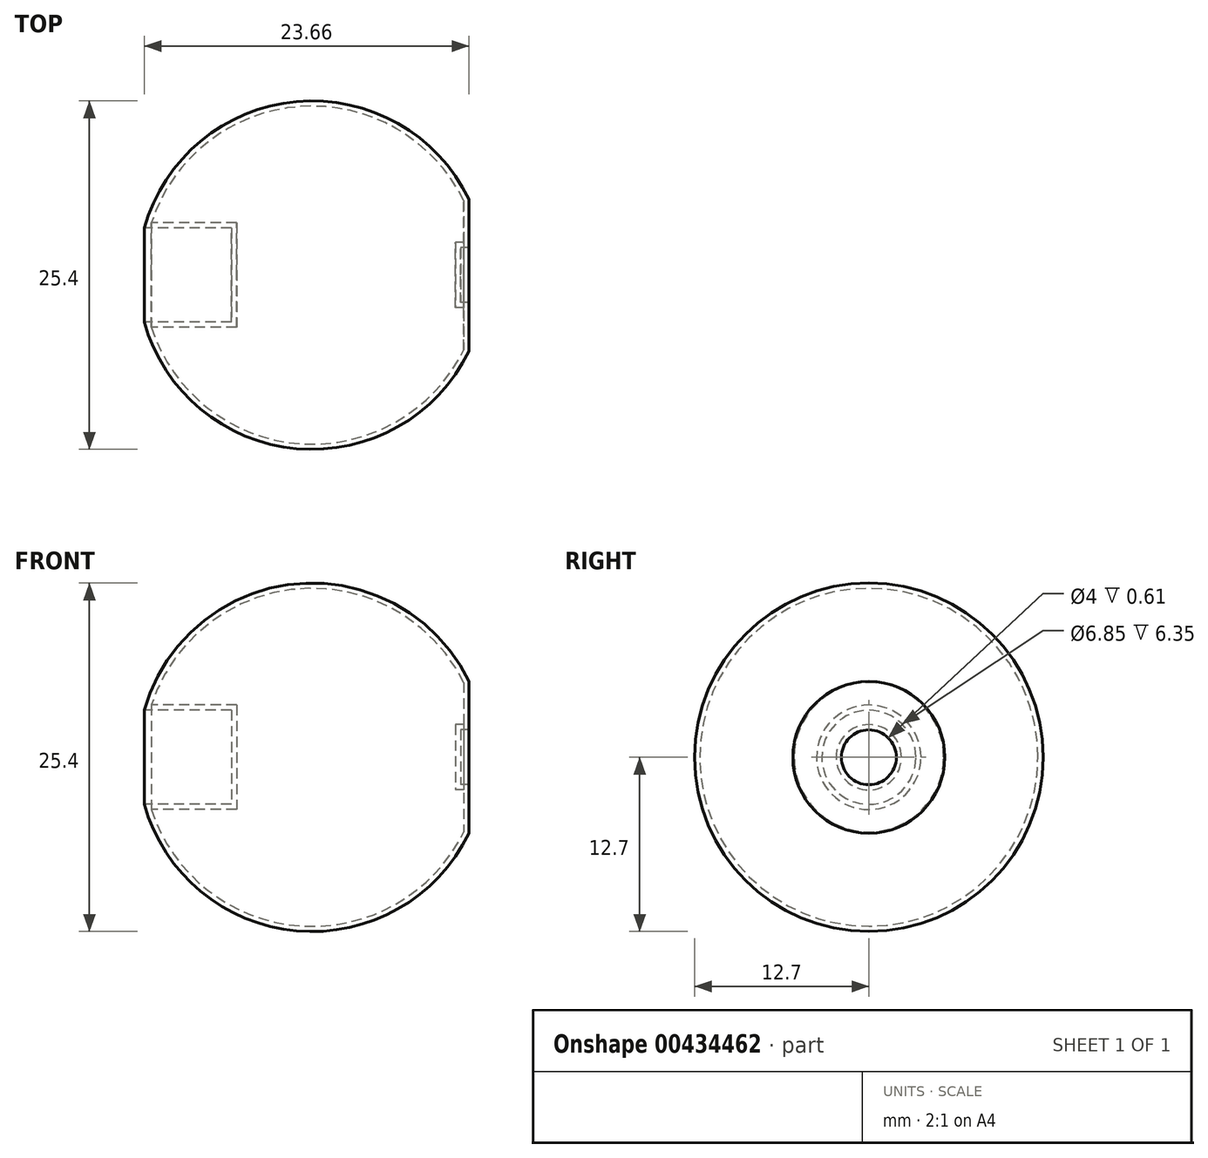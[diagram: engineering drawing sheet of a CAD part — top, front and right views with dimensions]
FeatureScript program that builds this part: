
annotation { "Feature Type Name" : "Feature", "Feature Type Description" : "" }
export const myFeature = defineFeature(function(context is Context, id is Id, definition is map)
    precondition{}
    {
        {
            var Q0;
            Q0=qCreatedBy(makeId("Front.planeOp"),FACE);
            var sketch = newSketch(context, id + "F0", { "sketchPlane" : qUnion([Q0])});
            skLineSegment(sketch, "E0", {"start": v(24.13, 2) * mm, "end": v(24.13, 5.54) * mm});
            skLineSegment(sketch, "E1", {"start": v(23.52, 0) * mm, "end": v(23.52, 2) * mm});
            skLineSegment(sketch, "E2", {"start": v(23.52, 2) * mm, "end": v(24.13, 2) * mm});
            skArc(sketch, "E3", {"start": v(24.13, 5.54) * mm, "mid": v(11.57, 12.65) * mm, "end": v(0.47, 3.43) * mm});
            skPoint(sketch, "E4.orphan", {"position": v(0, 0) * mm});
            skPoint(sketch, "E5.orphan", {"position": v(25.4, 0) * mm});
            skPoint(sketch, "E6.start.orphan", {"position": v(24.13, 0) * mm});
            skPoint(sketch, "E7.start.orphan", {"position": v(0.25, 0) * mm});
            skLineSegment(sketch, "E8.3", {"start": v(6.82, 0) * mm, "end": v(6.82, 1.53) * mm});
            skLineSegment(sketch, "E9", {"start": v(0.81, 0) * mm, "end": v(23.52, 0) * mm});
            skLineSegment(sketch, "E10", {"start": v(0.47, 3.43) * mm, "end": v(6.82, 3.43) * mm});
            skLineSegment(sketch, "E11", {"start": v(6.82, 0) * mm, "end": v(6.82, 3.43) * mm});
            skPoint(sketch, "E12.end.orphan", {"position": v(0.25, 1.27) * mm});
            skPoint(sketch, "E13.start.orphan", {"position": v(-7.48, 0) * mm});
            skLineSegment(sketch, "E14.0", {"start": v(7.2, 0) * mm, "end": v(7.2, 3.8) * mm});
            skLineSegment(sketch, "E14.1", {"start": v(0.98, 3.8) * mm, "end": v(7.2, 3.8) * mm});
            skLineSegment(sketch, "E14.2", {"start": v(23.14, 0) * mm, "end": v(23.14, 2.38) * mm});
            skLineSegment(sketch, "E14.3", {"start": v(23.14, 2.38) * mm, "end": v(23.75, 2.38) * mm});
            skLineSegment(sketch, "E14.4", {"start": v(23.75, 2.38) * mm, "end": v(23.75, 5.45) * mm});
            skArc(sketch, "E14.5", {"start": v(23.75, 5.45) * mm, "mid": v(11.81, 12.29) * mm, "end": v(0.98, 3.8) * mm});
            skSolve(sketch);
        }
        {
            var Q0;
            Q0=makeQuery(id+"F0.imprint","IMPRINT",FACE,{"disambiguationData":[TD([[makeQuery(id+"F0.imprint","IMPRINT",EDGE,{"derivedFrom":sQuery(id+"F0.wireOp",EDGE,"E0")}),1.0]])]});
            var Q1;
            Q1=sQuery(id+"F0.wireOp",EDGE,"E9");
            revolve(context, id + "F1", {"entities" : qUnion([Q0]), "axis" : qUnion([Q1]), "revolveType" : RevolveType.FULL});
        }
    });
